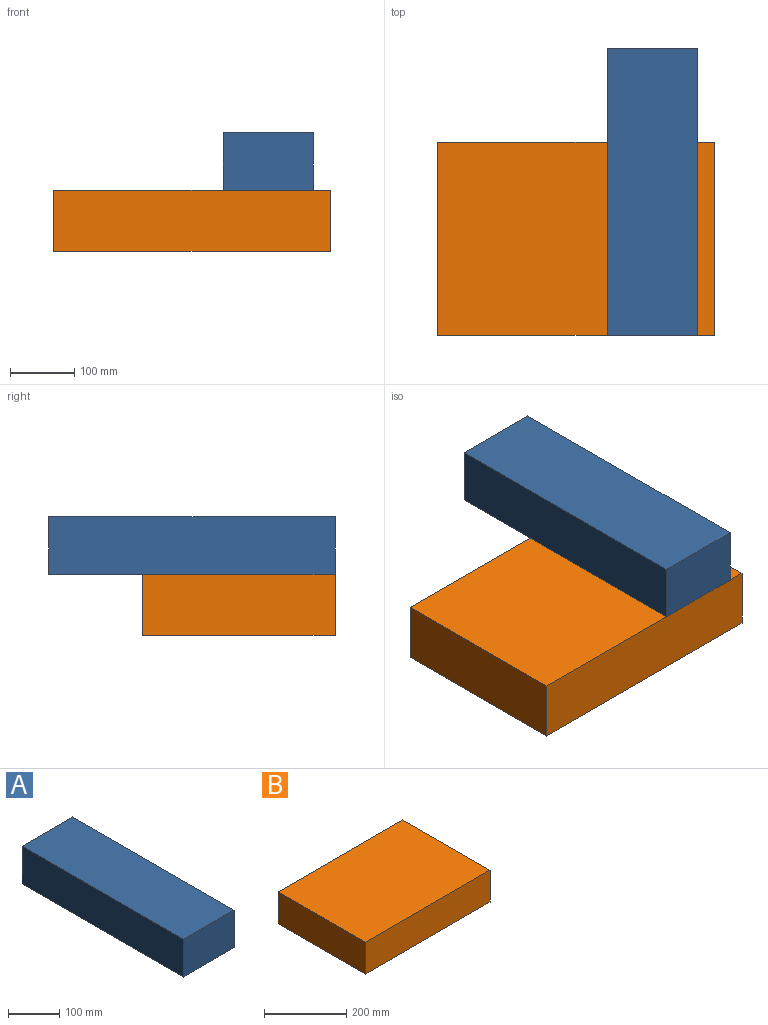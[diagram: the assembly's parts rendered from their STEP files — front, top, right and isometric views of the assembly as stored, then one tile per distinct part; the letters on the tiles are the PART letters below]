
ASSEMBLY  parts=2 mates=2
PART A: 6 faces, bbox 140x445x90 mm
  f0: plane 140x90mm, normal (0,-1,0), area 12600mm2, adj f1,f3,f4,f5
  f1: plane 445x90mm, normal (1,0,0), area 40050mm2, adj f0,f2,f4,f5
  f2: plane 140x90mm, normal (0,1,0), area 12600mm2, adj f1,f3,f4,f5
  f3: plane 445x90mm, normal (-1,0,0), area 40050mm2, adj f0,f2,f4,f5
  f4: plane 445x140mm, normal (0,0,1), area 62300mm2, adj f0,f1,f2,f3
  f5: plane 445x140mm, normal (0,0,-1), area 62300mm2, adj f0,f1,f2,f3
PART B: 6 faces, bbox 430x300x95 mm
  f0: plane 430x95mm, normal (0,-1,0), area 40850mm2, adj f1,f3,f4,f5
  f1: plane 300x95mm, normal (1,0,0), area 28500mm2, adj f0,f2,f4,f5
  f2: plane 430x95mm, normal (0,1,0), area 40850mm2, adj f1,f3,f4,f5
  f3: plane 300x95mm, normal (-1,0,0), area 28500mm2, adj f0,f2,f4,f5
  f4: plane 430x300mm, normal (0,0,1), area 129000mm2, adj f0,f1,f2,f3
  f5: plane 430x300mm, normal (0,0,-1), area 129000mm2, adj f0,f1,f2,f3
PLACE A t=(124.59,60.5,130.59)mm
PLACE B t=(5.69,-12,35.59)mm fixed
MATE planar A.f5 <-> B.f4  axis (0,0,-1) through (124.59,60.5,130.59)mm
MATE planar A.f0 <-> B.f0  axis (0,-1,0) through (124.59,-162,175.59)mm
